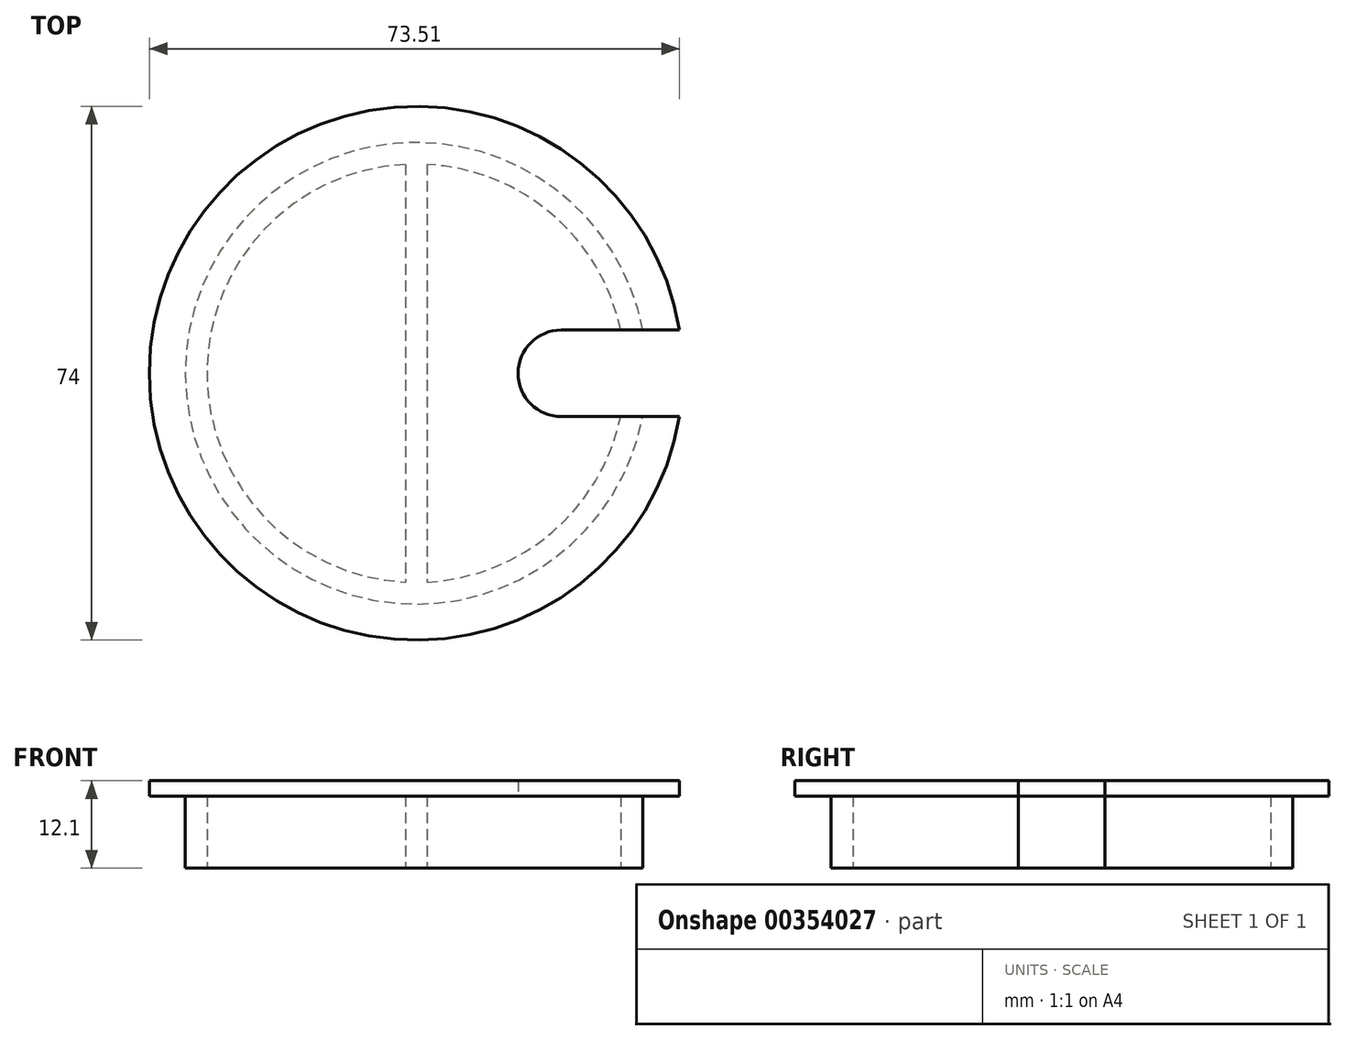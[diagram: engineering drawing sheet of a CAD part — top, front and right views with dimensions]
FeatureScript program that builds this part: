
annotation { "Feature Type Name" : "Feature", "Feature Type Description" : "" }
export const myFeature = defineFeature(function(context is Context, id is Id, definition is map)
    precondition{}
    {
        {
            var Q0;
            Q0=qCreatedBy(makeId("Top.planeOp"),FACE);
            var sketch = newSketch(context, id + "F0", { "sketchPlane" : qUnion([Q0])});
            skCircle(sketch, "E0", {"center": v(0, 0) * mm, "radius": 32 * mm});
            skArc(sketch, "E1.0", {"start": v(1.5, -28.96) * mm, "mid": v(29, 0) * mm, "end": v(1.5, 28.96) * mm});
            skLineSegment(sketch, "E2", {"start": v(-1.5, 28.96) * mm, "end": v(-1.5, -28.96) * mm});
            skLineSegment(sketch, "E3", {"start": v(1.5, 28.96) * mm, "end": v(1.5, -28.96) * mm});
            skArc(sketch, "E4.trimOffspring", {"start": v(-1.5, 28.96) * mm, "mid": v(-29, 0) * mm, "end": v(-1.5, -28.96) * mm});
            skSolve(sketch);
        }
        {
            var Q0;
            Q0 = qSketchRegion(id + "F0", true);
            extrude(context, id + "F1", {"entities" : qUnion([Q0]), "depth" : 10 * mm});
        }
        {
            var Q0;
            Q0=makeQuery(id+"F1.opExtrude","CAP_FACE",FACE,{"disambiguationData":[OSD([sQuery(id+"F0.wireOp",EDGE,"E0"),sQuery(id+"F0.wireOp",EDGE,"E1.0")])],"isStart":false});
            var sketch = newSketch(context, id + "F2", { "sketchPlane" : qUnion([Q0])});
            skCircle(sketch, "E5.0", {"center": v(0, 0) * mm, "radius": 32 * mm, "construction": true});
            skArc(sketch, "E6.0", {"start": v(36.51, 6) * mm, "mid": v(-37, 0) * mm, "end": v(36.51, -6) * mm});
            skArc(sketch, "E7", {"start": v(20.14, 6) * mm, "mid": v(14.14, 0) * mm, "end": v(20.14, -6) * mm});
            skLineSegment(sketch, "E8", {"start": v(20.14, 6) * mm, "end": v(36.51, 6) * mm});
            skLineSegment(sketch, "E9", {"start": v(20.14, -6) * mm, "end": v(36.51, -6) * mm});
            skSolve(sketch);
        }
        {
            var Q0;
            Q0 = qSketchRegion(id + "F2", true);
            extrude(context, id + "F3", {"entities" : qUnion([Q0]), "operationType" : NewBodyOperationType.ADD, "depth" : 2.1 * mm});
        }
        {
            var Q0;
            Q0=makeQuery(id+"F1.opExtrude","CAP_FACE",FACE,{"disambiguationData":[OSD([sQuery(id+"F0.wireOp",EDGE,"E0"),sQuery(id+"F0.wireOp",EDGE,"E1.0"),sQuery(id+"F0.wireOp",EDGE,"E2"),sQuery(id+"F0.wireOp",EDGE,"E3"),sQuery(id+"F0.wireOp",EDGE,"E4.trimOffspring")])],"isStart":false});
            var sketch = newSketch(context, id + "F4", { "sketchPlane" : qUnion([Q0])});
            skLineSegment(sketch, "E10.0", {"start": v(20.14, 6) * mm, "end": v(36.51, 6) * mm});
            skArc(sketch, "E11.0", {"start": v(20.14, 6) * mm, "mid": v(14.14, 0) * mm, "end": v(20.14, -6) * mm});
            skLineSegment(sketch, "E12.0", {"start": v(20.14, -6) * mm, "end": v(36.51, -6) * mm});
            skLineSegment(sketch, "E13", {"start": v(36.51, -6) * mm, "end": v(36.51, 6) * mm});
            skSolve(sketch);
        }
        {
            var Q0;
            Q0 = qSketchRegion(id + "F4", true);
            extrude(context, id + "F5", {"entities" : qUnion([Q0]), "operationType" : NewBodyOperationType.REMOVE, "oppositeDirection" : true, "depth" : 25 * mm});
        }
    });
